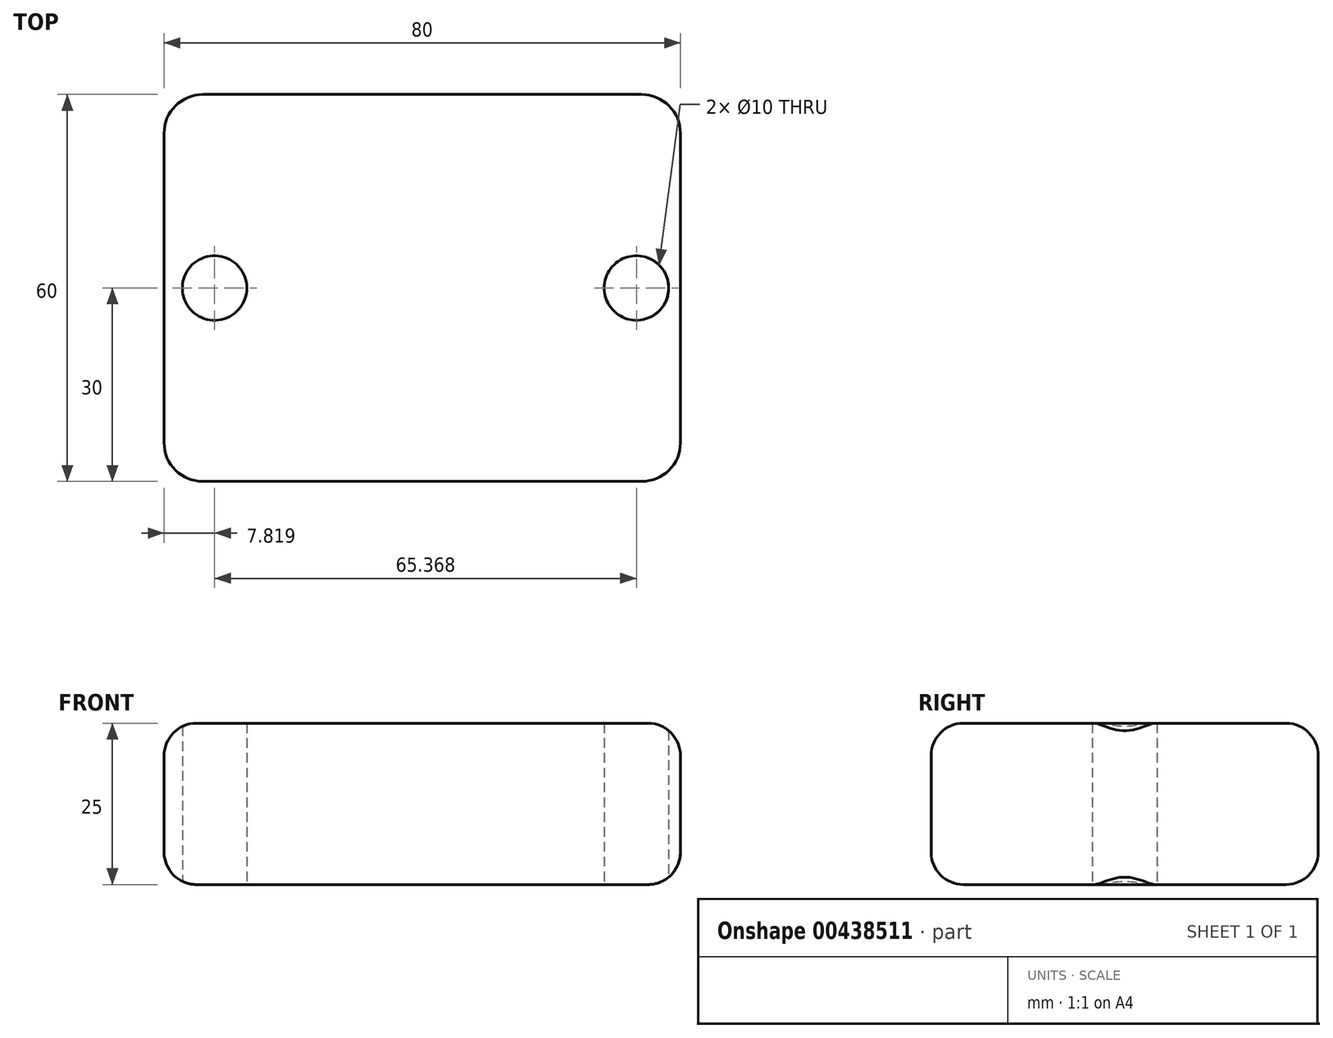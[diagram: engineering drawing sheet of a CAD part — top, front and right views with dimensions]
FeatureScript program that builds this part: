
annotation { "Feature Type Name" : "Feature", "Feature Type Description" : "" }
export const myFeature = defineFeature(function(context is Context, id is Id, definition is map)
    precondition{}
    {
        {
            var Q0;
            Q0=qCreatedBy(makeId("Top.planeOp"),FACE);
            var sketch = newSketch(context, id + "F0", { "sketchPlane" : qUnion([Q0])});
            skLineSegment(sketch, "E0.bottom", {"start": v(34, 30) * mm, "end": v(-34, 30) * mm});
            skLineSegment(sketch, "E0.top", {"start": v(34, -30) * mm, "end": v(-34, -30) * mm});
            skLineSegment(sketch, "E0.left", {"start": v(40, 24) * mm, "end": v(40, -24) * mm});
            skLineSegment(sketch, "E0.right", {"start": v(-40, 24) * mm, "end": v(-40, -24) * mm});
            skPoint(sketch, "E0.middle", {"position": v(0, 0) * mm});
            skPoint(sketch, "E1", {"position": v(-32.18, 0) * mm});
            skPoint(sketch, "E2", {"position": v(33.19, 0) * mm});
            skPoint(sketch, "E3.visualSharp", {"position": v(40, 30) * mm});
            skArc(sketch, "E3.filletArc", {"start": v(40, 24) * mm, "mid": v(38.24, 28.24) * mm, "end": v(34, 30) * mm});
            skPoint(sketch, "E4.visualSharp", {"position": v(-40, 30) * mm});
            skArc(sketch, "E4.filletArc", {"start": v(-34, 30) * mm, "mid": v(-38.24, 28.24) * mm, "end": v(-40, 24) * mm});
            skPoint(sketch, "E5.visualSharp", {"position": v(-40, -30) * mm});
            skArc(sketch, "E5.filletArc", {"start": v(-40, -24) * mm, "mid": v(-38.24, -28.24) * mm, "end": v(-34, -30) * mm});
            skPoint(sketch, "E6.visualSharp", {"position": v(40, -30) * mm});
            skArc(sketch, "E6.filletArc", {"start": v(34, -30) * mm, "mid": v(38.24, -28.24) * mm, "end": v(40, -24) * mm});
            skSolve(sketch);
        }
        {
            var Q0;
            Q0 = qSketchRegion(id + "F0", true);
            extrude(context, id + "F1", {"entities" : qUnion([Q0]), "depth" : 25 * mm});
        }
        {
            var Q0;
            Q0=sQuery(id+"F0.wireOp",VERTEX,"E1");
            var Q1;
            Q1=sQuery(id+"F0.wireOp",VERTEX,"E2");
            var Q2;
            Q2=makeQuery(id+"F1.opExtrude","SWEPT_BODY",BODY,{"disambiguationData":[OSD([sQuery(id+"F0.wireOp",EDGE,"E0.bottom"),sQuery(id+"F0.wireOp",EDGE,"E0.top"),sQuery(id+"F0.wireOp",EDGE,"E0.left"),sQuery(id+"F0.wireOp",EDGE,"E0.right")])]});
            hole(context, id + "F2", {"style" : HoleStyle.SIMPLE, "endStyle" : HoleEndStyle.THROUGH, "oppositeDirection" : true, "holeDiameter" : 10 * mm, "isTappedThrough" : true, "tappedDepth" : 12 * mm, "tapClearance" : 3, "locations" : qUnion([Q0, Q1]), "scope" : qUnion([Q2])});
        }
        {
            var Q0;
            Q0=makeQuery(id+"F1.opExtrude","CAP_EDGE",EDGE,{"disambiguationData":[OSD([sQuery(id+"F0.wireOp",EDGE,"E0.left")])],"isStart":false});
            var Q1;
            Q1=makeQuery(id+"F1.opExtrude","CAP_EDGE",EDGE,{"disambiguationData":[OSD([sQuery(id+"F0.wireOp",EDGE,"E0.top")])],"isStart":true});
            fillet(context, id + "F3", {"entities" : qUnion([Q0, Q1]), "radius" : 5 * mm, "tangentPropagation" : true, "allowEdgeOverflow" : false});
        }
    });
